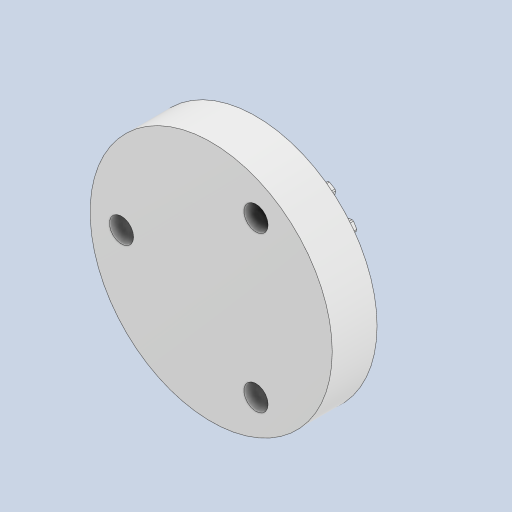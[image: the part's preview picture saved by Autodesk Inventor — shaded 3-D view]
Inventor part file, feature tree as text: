
AUTODESK INVENTOR PART (.ipt)
format: ipt  version: 2023 (Build 270158000, 158)  size: 308,736 bytes
history: native  units: mm (DEFAULTED — no unit token found)
features: extrude x3, plane x3, other x3, sketch x3, chamfer x1, fillet x1
ambient origin geometry x8: Origin, YZ Plane, XZ Plane, XY Plane, X Axis, Y Axis, Z Axis, Center Point
bodies: Solid1 (feature_tree)
feature tree (14):
  extrude  "Extrusion1"  Depth=5.0mm TaperAngle=0.0deg
  plane  "Work Plane2"
  plane  "Work Plane8"
  plane  "Work Plane9"
  other  "平歯車"
  sketch  "スケッチ5"
  extrude  "押し出し3"  Depth=10.0mm TaperAngle=0.0deg
  extrude  "押し出し4"  Depth=0.3mm
  chamfer  "面取り1"  Angle=15.0deg  [1 undecoded]
  fillet  "フィレット1"  [1 undecoded]
  sketch  "Sketch1"  dims[d0=14.0mm d1=5.0mm d2=0.0mm]
  sketch  "Sketch2"  dims[d3=12.0mm d4=10.0mm d5=0.0mm d16=12.0mm d17=0.0mm d34=15.0deg d39=0.0mm d41=0.0mm d43=12.0mm d46=12.0mm d47=0.0mm d48=0.0mm d51=27.0mm d52=5.0mm d53=2.7mm d54=10.0mm d55=30.0mm d57=360.0deg d59=5.0mm d60=0.0mm d61=3.0mm d62=0.0mm d63=0.1mm d64=2.0mm d65=45.0deg d66=0.3mm]
  other  "Srf1"
  other  "ピッチ円直径"
note: 2 required parameter values undecoded (feature->parameter linkage not recoverable at this tier; creation-order binding heuristic only, values carry confidence <= 0.55)
